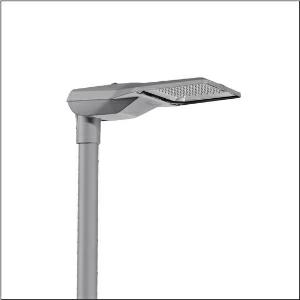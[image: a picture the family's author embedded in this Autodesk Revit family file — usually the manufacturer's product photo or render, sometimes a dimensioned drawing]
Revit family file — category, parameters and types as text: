
# Revit family: streetlight_sl_21_midi___pc-r_5xe3g33s08mb_c3de
name_source: partatom
category: Lighting Fixtures
units: mm (PartAtom-declared; Revit-internal decimal feet)

## family parameters
Cut with Voids When Loaded = No
Host = Face
Light Source = No
Part Type = Normal
Room Calculation Point = No
Round Connector Dimension = Use Diameter
Shared = No

## types (1)
- --- (1 x LED, 17390 lm, 136 W, 3000K)
    Apparent Load = 136 VA
    CIE Flux Codes = 38 78 98 100 100
    Color Rendering = 70
    Color Temperature = 3000K
    Default Elevation = 1800 mm
    Description = Streetlight SL 21 midi, mast luminaire, primary light control with lens, of PMMA, primary optical cover: cover, of toughened safety glass, transparent, light distribution: PC-R, light emission: direct distribution, primary light characteristic: asymmetric, right, installation type: side-entry, post-top, LED, High Power LED, rated luminous flux: 17.390lm, luminous efficacy: 128lm/W, light colour: 730, colour temperature: 3000K, control: overheat protection, constant luminous flux control, time-dependent luminous flux control, flexible luminous flux parameterisation, presetting dimming logarithmic, mains connection: 230..240V, AC, 50/60Hz, start of lifetime: 136W, end of service life: 142W, reduction: 61W, luminaire housing, of diecast aluminium, powder-coated, Siteco® metallic grey (DB 702S), corrosivity category C5 mid according to DIN EN ISO 12944, please order mast flange separately, inclination adjustable: 0°, 5°, 10°, 15°, sealing non-destructively replaceable, multi-level sealing system, length: 644mm, width: 335mm, height: 110mm, mast flange for spigot size: 42mm (side-entry): 5XC10008XM4, 60/48mm (side-entry/post-top): 5XC10108XM2, 76/60mm (side-entry/post-top): 5XC10108XM1, Smart Interface above, protection rating (complete): IP66, insulation class (complete): insulation class II (safety insulation), certification: CE, ENEC, ENEC+, VDE, impact resistance: IK09, permissible operating ambient temperature for outdoor applications: -40..+50°C, standard-compliant lighting for roads and squares, packaging unit: 1 piece

Light Distribution: PC-R
    Height = 111 mm
    Lamp = 1 x LED
    Lamp Light Flux = 17390 lm
    Lamp Power = 136 W
    Lamp count = 1
    Length = 644 mm
    Luminous efficacy = 128 lm/W
    Manufacturer = Siteco
    ModVariant = No
    Model = 5XE3G33S08MB
    Number of Poles = 1
    OnlyDefault = Yes
    Power Factor = 1
    Product Name = Streetlight SL 21 midi | PC-R
    Product group = mast luminaire | pylon top
    ProductGroupID = 6100
    Protection Class = Protection class II
    Protection Degree = IP 66
    RLX_Detail_Level = 1
    RLX_Emergency_Light_Flux = 0 lm
    RLX_Emergency_Type = 0
    RLX_Emergency_Type_DB = No
    RlxData = <blob elided: 93013 chars, md5=49d9b51e>
    Socket = socket
    Standby Power = 0 W
    System Light Flux = 17390 lm
    System Power = 136 W
    Type Comments = factory setting: luminous flux: 100 % | dim-lin: 254 | 695 mA
    Type Image = l_1004302.jpg
    URL = http://relux.com
    VarID = @adj_022913
    Voltage = 0 V
    Weight = 0.00 kg
    Width = 336 mm

## geometry (parser evidence)
native form markers: Blend x4, Sweep x10
no freeform markers — native parametric forms only
